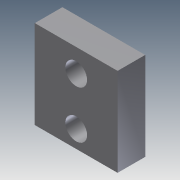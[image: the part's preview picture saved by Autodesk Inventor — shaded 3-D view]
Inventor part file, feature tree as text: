
AUTODESK INVENTOR PART (.ipt)
format: ipt  version: 2011 (Build 150239000, 239)  size: 84,480 bytes
history: native  units: in
note: dims shown in document units (in); Inventor stores cm internally (conversion verified against a paired STEP export)
features: extrude x2, sketch x2
ambient origin geometry x8: Origin, YZ Plane, XZ Plane, XY Plane, X Axis, Y Axis, Z Axis, Center Point
bodies: Solid1 (feature_tree)
feature tree (4):
  extrude  "Extrusion1"  Depth=1.6in
  extrude  "Extrusion2"  Depth=0.315in
  sketch  "Sketch1"  dims[d0=1.5in d1=1.6in]
  sketch  "Sketch2"  dims[d2=0.5in d3=0.0in d4=0.315in d5=0.3937in d6=1.1811in d7=0.5in d8=0.0in]
